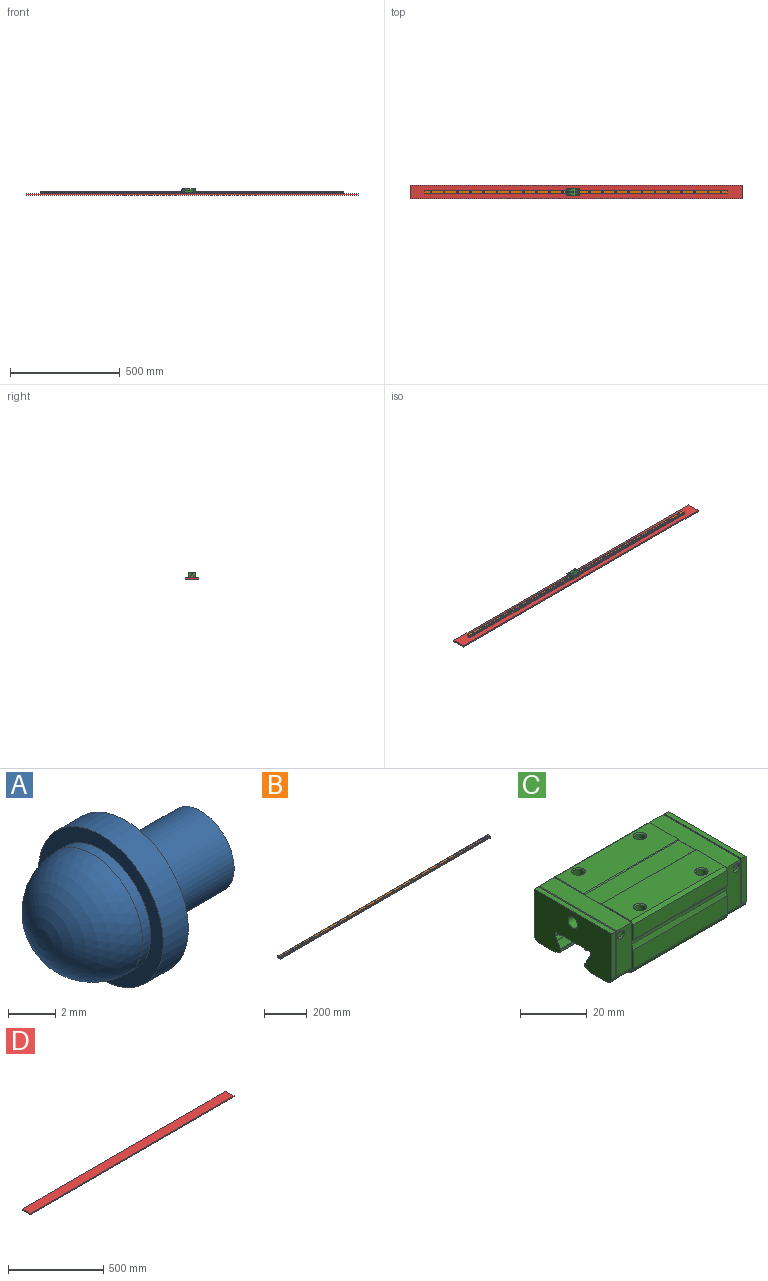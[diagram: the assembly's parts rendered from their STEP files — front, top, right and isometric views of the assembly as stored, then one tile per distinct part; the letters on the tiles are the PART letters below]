
ASSEMBLY  parts=4 mates=3
PART A: 7 faces, bbox 9.5x7.5x7.5 mm
  f0: sphere r=3mm, area 56.5mm2, adj f1
  f1: cylinder r=3mm len=6mm, axis (1,0,0), area 9.4mm2, adj f0,f2
  f2: plane 7.5x7.5mm, normal (-1,0,0), area 15.9mm2, adj f1,f3
  f3: cylinder r=3.75mm len=7.5mm, axis (1,0,0), area 35.3mm2, adj f2,f4
  f4: plane 7.5x7.5mm, normal (1,0,0), area 31.6mm2, adj f3,f5
  f5: cylinder r=2mm len=4.5mm, axis (1,0,0), area 56.5mm2, adj f4,f6
  f6: plane 4x4mm, normal (1,0,0), area 12.6mm2, adj f5
PART B: 97 faces, bbox 1380x15x12.5 mm
  f0: plane 1380x3.92mm, normal (0,-1,0), area 5405.5mm2, adj f1,f25,f26,f27
  f1: plane 1380x0.85mm, normal (0,-0.71,-0.71), area 1658.9mm2, adj f0,f2,f26,f27
  f2: plane 1380x13.3mm, normal (0,0,-1), area 17988.2mm2, adj f1,f3,f26,f27,f30,f33,f36,f39
  f3: plane 1380x0.85mm, normal (0,0.71,-0.71), area 1658.9mm2, adj f2,f4,f26,f27
  f4: plane 1380x3.92mm, normal (0,1,0), area 5405.5mm2, adj f3,f5,f26,f27
  f5: plane 1380x1.85mm, normal (0,0.52,0.86), area 2989.3mm2, adj f4,f6,f26,f27
  f6: cylinder r=0.7mm len=1380mm, axis (-1,0,0), area 1858.8mm2, adj f5,f7,f26,f27
  f7: cylinder r=0.7mm len=1380mm, axis (-1,0,0), area 462mm2, adj f6,f8,f26,f27
  f8: plane 1380x2.43mm, normal (0,0.87,-0.5), area 3876.2mm2, adj f7,f9,f26,f27
  f9: cylinder r=1.45mm len=1380mm, axis (-1,0,0), area 1949.3mm2, adj f8,f10,f26,f27
  f10: plane 1380x0.16mm, normal (0,0.85,-0.52), area 253.7mm2, adj f9,f11,f26,f27
  f11: plane 1380x1.08mm, normal (0,1,0), area 1490.4mm2, adj f10,f12,f26,f27
  f12: plane 1380x0.45mm, normal (0,0.71,0.71), area 878.2mm2, adj f11,f13,f26,f27
  f13: plane 1380x0.38mm, normal (0,0,1), area 529.8mm2, adj f12,f14,f26,f27
  f14: cylinder r=1.45mm len=1380mm, axis (-1,0,0), area 2719.1mm2, adj f13,f15,f26,f27
  f15: plane 1380x9.69mm, normal (0,0,1), area 12353mm2, adj f14,f16,f26,f27,f28,f31,f34,f37
  f16: cylinder r=1.45mm len=1380mm, axis (-1,0,0), area 2719.1mm2, adj f15,f17,f26,f27
  f17: plane 1380x0.38mm, normal (0,0,1), area 529.8mm2, adj f16,f18,f26,f27
  f18: plane 1380x0.45mm, normal (0,-0.71,0.71), area 878.2mm2, adj f17,f19,f26,f27
  f19: plane 1380x1.08mm, normal (0,-1,0), area 1490.4mm2, adj f18,f20,f26,f27
  f20: plane 1380x0.16mm, normal (0,-0.85,-0.52), area 253.7mm2, adj f19,f21,f26,f27
  f21: cylinder r=1.45mm len=1380mm, axis (-1,0,0), area 1949.3mm2, adj f20,f22,f26,f27
  f22: plane 1380x2.43mm, normal (0,-0.87,-0.5), area 3876.2mm2, adj f21,f23,f26,f27
  f23: cylinder r=0.7mm len=1380mm, axis (-1,0,0), area 462mm2, adj f22,f24,f26,f27
  f24: cylinder r=0.7mm len=1380mm, axis (-1,0,0), area 1858.8mm2, adj f23,f25,f26,f27
  f25: plane 1380x1.85mm, normal (0,-0.52,0.86), area 2989.3mm2, adj f0,f24,f26,f27
  f26: plane 15x12.5mm, normal (1,0,0), area 168.5mm2, adj f0,f1,f2,f3,f4,f5,f6,f7
  f27: plane 15x12.5mm, normal (-1,0,0), area 168.5mm2, adj f0,f1,f2,f3,f4,f5,f6,f7
  f28: cylinder r=3.75mm len=7.5mm, axis (0,0,-1), area 124.9mm2, adj f15,f29
  f29: plane 7.5x7.5mm, normal (0,0,1), area 28.3mm2, adj f28,f30
  f30: cylinder r=2.25mm len=7.2mm, axis (0,0,-1), area 101.8mm2, adj f2,f29
  f31: cylinder r=3.75mm len=7.5mm, axis (0,0,-1), area 124.9mm2, adj f15,f32
  f32: plane 7.5x7.5mm, normal (0,0,1), area 28.3mm2, adj f31,f33
  f33: cylinder r=2.25mm len=7.2mm, axis (0,0,-1), area 101.8mm2, adj f2,f32
  f34: cylinder r=3.75mm len=7.5mm, axis (0,0,-1), area 124.9mm2, adj f15,f35
  f35: plane 7.5x7.5mm, normal (0,0,1), area 28.3mm2, adj f34,f36
  f36: cylinder r=2.25mm len=7.2mm, axis (0,0,-1), area 101.8mm2, adj f2,f35
  f37: cylinder r=3.75mm len=7.5mm, axis (0,0,-1), area 124.9mm2, adj f15,f38
  f38: plane 7.5x7.5mm, normal (0,0,1), area 28.3mm2, adj f37,f39
  f39: cylinder r=2.25mm len=7.2mm, axis (0,0,-1), area 101.8mm2, adj f2,f38
  f40: cylinder r=3.75mm len=7.5mm, axis (0,0,-1), area 124.9mm2, adj f15,f41
  f41: plane 7.5x7.5mm, normal (0,0,1), area 28.3mm2, adj f40,f42
  f42: cylinder r=2.25mm len=7.2mm, axis (0,0,-1), area 101.8mm2, adj f2,f41
  f43: cylinder r=3.75mm len=7.5mm, axis (0,0,-1), area 124.9mm2, adj f15,f44
  f44: plane 7.5x7.5mm, normal (0,0,1), area 28.3mm2, adj f43,f45
  f45: cylinder r=2.25mm len=7.2mm, axis (0,0,-1), area 101.8mm2, adj f2,f44
  f46: cylinder r=3.75mm len=7.5mm, axis (0,0,-1), area 124.9mm2, adj f15,f47
  f47: plane 7.5x7.5mm, normal (0,0,1), area 28.3mm2, adj f46,f48
  f48: cylinder r=2.25mm len=7.2mm, axis (0,0,-1), area 101.8mm2, adj f2,f47
  f49: cylinder r=3.75mm len=7.5mm, axis (0,0,-1), area 124.9mm2, adj f15,f50
  f50: plane 7.5x7.5mm, normal (0,0,1), area 28.3mm2, adj f49,f51
  f51: cylinder r=2.25mm len=7.2mm, axis (0,0,-1), area 101.8mm2, adj f2,f50
  f52: cylinder r=3.75mm len=7.5mm, axis (0,0,-1), area 124.9mm2, adj f15,f53
  f53: plane 7.5x7.5mm, normal (0,0,1), area 28.3mm2, adj f52,f54
  f54: cylinder r=2.25mm len=7.2mm, axis (0,0,-1), area 101.8mm2, adj f2,f53
  f55: cylinder r=3.75mm len=7.5mm, axis (0,0,-1), area 124.9mm2, adj f15,f56
  f56: plane 7.5x7.5mm, normal (0,0,1), area 28.3mm2, adj f55,f57
  f57: cylinder r=2.25mm len=7.2mm, axis (0,0,-1), area 101.8mm2, adj f2,f56
  f58: cylinder r=3.75mm len=7.5mm, axis (0,0,-1), area 124.9mm2, adj f15,f59
  f59: plane 7.5x7.5mm, normal (0,0,1), area 28.3mm2, adj f58,f60
  f60: cylinder r=2.25mm len=7.2mm, axis (0,0,-1), area 101.8mm2, adj f2,f59
  f61: cylinder r=3.75mm len=7.5mm, axis (0,0,-1), area 124.9mm2, adj f15,f62
  f62: plane 7.5x7.5mm, normal (0,0,1), area 28.3mm2, adj f61,f63
  f63: cylinder r=2.25mm len=7.2mm, axis (0,0,-1), area 101.8mm2, adj f2,f62
  f64: cylinder r=3.75mm len=7.5mm, axis (0,0,-1), area 124.9mm2, adj f15,f65
  f65: plane 7.5x7.5mm, normal (0,0,1), area 28.3mm2, adj f64,f66
  f66: cylinder r=2.25mm len=7.2mm, axis (0,0,-1), area 101.8mm2, adj f2,f65
  f67: cylinder r=3.75mm len=7.5mm, axis (0,0,-1), area 124.9mm2, adj f15,f68
  f68: plane 7.5x7.5mm, normal (0,0,1), area 28.3mm2, adj f67,f69
  f69: cylinder r=2.25mm len=7.2mm, axis (0,0,-1), area 101.8mm2, adj f2,f68
  f70: cylinder r=3.75mm len=7.5mm, axis (0,0,-1), area 124.9mm2, adj f15,f71
  f71: plane 7.5x7.5mm, normal (0,0,1), area 28.3mm2, adj f70,f72
  f72: cylinder r=2.25mm len=7.2mm, axis (0,0,-1), area 101.8mm2, adj f2,f71
  f73: cylinder r=3.75mm len=7.5mm, axis (0,0,-1), area 124.9mm2, adj f15,f74
  f74: plane 7.5x7.5mm, normal (0,0,1), area 28.3mm2, adj f73,f75
  f75: cylinder r=2.25mm len=7.2mm, axis (0,0,-1), area 101.8mm2, adj f2,f74
  f76: cylinder r=3.75mm len=7.5mm, axis (0,0,-1), area 124.9mm2, adj f15,f77
  f77: plane 7.5x7.5mm, normal (0,0,1), area 28.3mm2, adj f76,f78
  f78: cylinder r=2.25mm len=7.2mm, axis (0,0,-1), area 101.8mm2, adj f2,f77
  f79: cylinder r=3.75mm len=7.5mm, axis (0,0,-1), area 124.9mm2, adj f15,f80
  f80: plane 7.5x7.5mm, normal (0,0,1), area 28.3mm2, adj f79,f81
  f81: cylinder r=2.25mm len=7.2mm, axis (0,0,-1), area 101.8mm2, adj f2,f80
  f82: cylinder r=3.75mm len=7.5mm, axis (0,0,-1), area 124.9mm2, adj f15,f83
  f83: plane 7.5x7.5mm, normal (0,0,1), area 28.3mm2, adj f82,f84
  f84: cylinder r=2.25mm len=7.2mm, axis (0,0,-1), area 101.8mm2, adj f2,f83
  f85: cylinder r=3.75mm len=7.5mm, axis (0,0,-1), area 124.9mm2, adj f15,f86
  f86: plane 7.5x7.5mm, normal (0,0,1), area 28.3mm2, adj f85,f87
  f87: cylinder r=2.25mm len=7.2mm, axis (0,0,-1), area 101.8mm2, adj f2,f86
  f88: cylinder r=3.75mm len=7.5mm, axis (0,0,-1), area 124.9mm2, adj f15,f89
  f89: plane 7.5x7.5mm, normal (0,0,1), area 28.3mm2, adj f88,f90
  f90: cylinder r=2.25mm len=7.2mm, axis (0,0,-1), area 101.8mm2, adj f2,f89
  f91: cylinder r=3.75mm len=7.5mm, axis (0,0,-1), area 124.9mm2, adj f15,f92
  f92: plane 7.5x7.5mm, normal (0,0,1), area 28.3mm2, adj f91,f93
  f93: cylinder r=2.25mm len=7.2mm, axis (0,0,-1), area 101.8mm2, adj f2,f92
  f94: cylinder r=3.75mm len=7.5mm, axis (0,0,-1), area 124.9mm2, adj f15,f95
  f95: plane 7.5x7.5mm, normal (0,0,1), area 28.3mm2, adj f94,f96
  f96: cylinder r=2.25mm len=7.2mm, axis (0,0,-1), area 101.8mm2, adj f2,f95
PART C: 100 faces, bbox 56.9x34x19.5 mm
  f0: plane 16.6x6.3mm, normal (0,-1,0), area 97.5mm2, adj f4,f15,f24,f76,f98
  f1: plane 16.6x1.7mm, normal (0,-1,0), area 28.2mm2, adj f4,f25,f31,f73
  f2: plane 16.6x6.3mm, normal (0,1,0), area 97.5mm2, adj f5,f15,f24,f80,f99
  f3: plane 16.6x1.7mm, normal (0,1,0), area 28.2mm2, adj f5,f25,f31,f73
  f4: cylinder r=2mm len=8.5mm, axis (1,0,0), area 26.2mm2, adj f0,f1,f15,f30,f31,f73,f98
  f5: cylinder r=2mm len=8.5mm, axis (1,0,0), area 26.2mm2, adj f2,f3,f15,f29,f31,f73,f99
  f6: plane 32.8x0.5mm, normal (0.71,0,0.71), area 22.8mm2, adj f24,f73,f98,f99
  f7: plane 16.6x6.3mm, normal (0,-1,0), area 97.5mm2, adj f11,f14,f27,f74,f97
  f8: plane 16.6x1.7mm, normal (0,-1,0), area 28.2mm2, adj f11,f26,f28,f72
  f9: plane 16.6x1.7mm, normal (0,1,0), area 28.2mm2, adj f12,f26,f28,f72
  f10: plane 16.6x6.3mm, normal (0,1,0), area 97.5mm2, adj f12,f14,f27,f78,f96
  f11: cylinder r=2mm len=8.5mm, axis (-1,0,0), area 26.2mm2, adj f7,f8,f14,f28,f30,f72,f97
  f12: cylinder r=2mm len=8.5mm, axis (-1,0,0), area 26.2mm2, adj f9,f10,f14,f28,f29,f72,f96
  f13: plane 32.8x0.5mm, normal (-0.71,0,0.71), area 22.8mm2, adj f27,f72,f96,f97
  f14: plane 34x19.5mm, normal (-1,0,0), area 38.1mm2, adj f7,f10,f11,f12,f16,f17,f20,f21
  f15: plane 34x19.5mm, normal (1,0,0), area 38.1mm2, adj f0,f2,f4,f5,f16,f17,f20,f21
  f16: plane 39.9x5.95mm, normal (0,0,-1), area 237.2mm2, adj f14,f15,f33,f94
  f17: plane 39.9x5.95mm, normal (0,0,-1), area 237.2mm2, adj f14,f15,f34,f95
  f18: plane 56.9x1.47mm, normal (0,-0.52,-0.86), area 97.6mm2, adj f28,f29,f31,f53
  f19: plane 56.9x1.47mm, normal (0,0.52,-0.86), area 97.6mm2, adj f28,f30,f31,f71
  f20: plane 39.9x6.69mm, normal (0,-1,0), area 266.9mm2, adj f14,f15,f33,f92
  f21: plane 39.9x5.52mm, normal (0,-1,0), area 220.2mm2, adj f14,f15,f32,f93
  f22: plane 39.9x6.69mm, normal (0,1,0), area 266.9mm2, adj f14,f15,f34,f88
  f23: plane 39.9x5.52mm, normal (0,1,0), area 220.2mm2, adj f14,f15,f35,f89
  f24: plane 32.8x6.3mm, normal (0,0,1), area 206.6mm2, adj f0,f2,f6,f15
  f25: plane 32.8x1.7mm, normal (0,0,1), area 55.8mm2, adj f1,f3,f31,f73
  f26: plane 32.8x1.7mm, normal (0,0,1), area 55.8mm2, adj f8,f9,f28,f72
  f27: plane 32.8x6.3mm, normal (0,0,1), area 206.6mm2, adj f7,f10,f13,f14
  f28: plane 32.8x18.6mm, normal (-1,0,0), area 501.5mm2, adj f8,f9,f11,f12,f18,f19,f26,f29
  f29: plane 56.9x7.29mm, normal (0,0,-1), area 146.6mm2, adj f5,f12,f14,f15,f18,f28,f31,f95
  f30: plane 56.9x7.29mm, normal (0,0,-1), area 146.6mm2, adj f4,f11,f14,f15,f19,f28,f31,f94
  f31: plane 32.8x18.6mm, normal (1,0,0), area 501.5mm2, adj f1,f3,f4,f5,f18,f19,f25,f29
  f32: plane 39.9x0.98mm, normal (0,-0.71,0.71), area 55.3mm2, adj f14,f15,f21,f40
  f33: cylinder r=2.5mm len=39.9mm, axis (-1,0,0), area 156.7mm2, adj f14,f15,f16,f20
  f34: cylinder r=2.5mm len=39.9mm, axis (-1,0,0), area 156.7mm2, adj f14,f15,f17,f22
  f35: plane 39.9x0.98mm, normal (0,0.71,0.71), area 55.3mm2, adj f14,f15,f23,f36
  f36: plane 39.9x12.22mm, normal (0,0,1), area 462.4mm2, adj f14,f15,f35,f37,f47,f50
  f37: plane 39.9x0.3mm, normal (0,-0.71,0.71), area 16.9mm2, adj f14,f15,f36,f38
  f38: plane 39.9x7mm, normal (0,0,1), area 279.3mm2, adj f14,f15,f37,f39
  f39: plane 39.9x0.3mm, normal (0,0.71,0.71), area 16.9mm2, adj f14,f15,f38,f40
  f40: plane 39.9x12.22mm, normal (0,0,1), area 462.4mm2, adj f14,f15,f32,f39,f41,f44
  f41: cone r=2mm half-angle=45deg, axis (0,0,1), area 6.1mm2, adj f40,f42
  f42: cylinder r=1.62mm len=8.02mm, axis (0,0,-1), area 81.7mm2, adj f41,f43
  f43: cone r=1.62mm half-angle=60deg, axis (0,0,1), area 9.5mm2, adj f42
  f44: cone r=2mm half-angle=45deg, axis (0,0,1), area 6.1mm2, adj f40,f45
  f45: cylinder r=1.62mm len=8.02mm, axis (0,0,-1), area 81.7mm2, adj f44,f46
  f46: cone r=1.62mm half-angle=60deg, axis (0,0,1), area 9.5mm2, adj f45
  f47: cone r=2mm half-angle=45deg, axis (0,0,1), area 6.1mm2, adj f36,f48
  f48: cylinder r=1.62mm len=8.02mm, axis (0,0,-1), area 81.7mm2, adj f47,f49
  f49: cone r=1.62mm half-angle=60deg, axis (0,0,1), area 9.5mm2, adj f48
  f50: cone r=2mm half-angle=45deg, axis (0,0,1), area 6.1mm2, adj f36,f51
  f51: cylinder r=1.62mm len=8.02mm, axis (0,0,-1), area 81.7mm2, adj f50,f52
  f52: cone r=1.62mm half-angle=60deg, axis (0,0,1), area 9.5mm2, adj f51
  f53: cylinder r=0.7mm len=56.9mm, axis (-1,0,0), area 76.6mm2, adj f18,f28,f31,f54
  f54: cylinder r=0.7mm len=56.9mm, axis (-1,0,0), area 19mm2, adj f28,f31,f53,f55
  f55: plane 56.9x2.43mm, normal (0,-0.87,0.5), area 159.8mm2, adj f28,f31,f54,f56
  f56: cylinder r=1.45mm len=56.9mm, axis (-1,0,0), area 80.4mm2, adj f28,f31,f55,f57
  f57: plane 56.9x0.16mm, normal (0,-0.85,0.52), area 10.5mm2, adj f28,f31,f56,f58
  f58: plane 56.9x1.08mm, normal (0,-1,0), area 61.5mm2, adj f28,f31,f57,f59
  f59: plane 56.9x0.45mm, normal (0,-0.71,-0.71), area 36.2mm2, adj f28,f31,f58,f60
  f60: plane 56.9x0.38mm, normal (0,0,-1), area 21.8mm2, adj f28,f31,f59,f61
  f61: cylinder r=1.45mm len=56.9mm, axis (-1,0,0), area 112.1mm2, adj f28,f31,f60,f62
  f62: plane 56.9x9.69mm, normal (0,0,-1), area 551.2mm2, adj f28,f31,f61,f63
  f63: cylinder r=1.45mm len=56.9mm, axis (-1,0,0), area 112.1mm2, adj f28,f31,f62,f64
  f64: plane 56.9x0.38mm, normal (0,0,-1), area 21.8mm2, adj f28,f31,f63,f65
  f65: plane 56.9x0.45mm, normal (0,0.71,-0.71), area 36.2mm2, adj f28,f31,f64,f66
  f66: plane 56.9x1.08mm, normal (0,1,0), area 61.5mm2, adj f28,f31,f65,f67
  f67: plane 56.9x0.16mm, normal (0,0.85,0.52), area 10.5mm2, adj f28,f31,f66,f68
  f68: cylinder r=1.45mm len=56.9mm, axis (-1,0,0), area 80.4mm2, adj f28,f31,f67,f69
  f69: plane 56.9x2.43mm, normal (0,0.87,0.5), area 159.8mm2, adj f28,f31,f68,f70
  f70: cylinder r=0.7mm len=56.9mm, axis (-1,0,0), area 19mm2, adj f28,f31,f69,f71
  f71: cylinder r=0.7mm len=56.9mm, axis (-1,0,0), area 76.6mm2, adj f19,f28,f31,f70
  f72: plane 32.8x17.92mm, normal (1,0,0), area 33.4mm2, adj f8,f9,f11,f12,f13,f26,f96,f97
  f73: plane 32.8x17.92mm, normal (-1,0,0), area 33.4mm2, adj f1,f3,f4,f5,f6,f25,f98,f99
  f74: cylinder r=1.5mm len=3mm, axis (0,-1,0), area 9.4mm2, adj f7,f75
  f75: plane 3x3mm, normal (0,-1,0), area 7.1mm2, adj f74
  f76: cylinder r=1.5mm len=3mm, axis (0,-1,0), area 9.4mm2, adj f0,f77
  f77: plane 3x3mm, normal (0,-1,0), area 7.1mm2, adj f76
  f78: cylinder r=1.5mm len=3mm, axis (0,1,0), area 9.4mm2, adj f10,f79
  f79: plane 3x3mm, normal (0,1,0), area 7.1mm2, adj f78
  f80: cylinder r=1.5mm len=3mm, axis (0,1,0), area 9.4mm2, adj f2,f81
  f81: plane 3x3mm, normal (0,1,0), area 7.1mm2, adj f80
  f82: cylinder r=2mm len=4.5mm, axis (1,0,0), area 56.5mm2, adj f28,f83
  f83: plane 4x4mm, normal (-1,0,0), area 12.6mm2, adj f82
  f84: plane 4x4mm, normal (1,0,0), area 12.6mm2, adj f85
  f85: cylinder r=2mm len=4.5mm, axis (1,0,0), area 56.5mm2, adj f31,f84
  f86: plane 39.9x1.13mm, normal (0,1,0), area 45.2mm2, adj f14,f15,f87,f88
  f87: cylinder r=0.5mm len=39.9mm, axis (-1,0,0), area 12.2mm2, adj f14,f15,f86,f89
  f88: plane 39.9x1.81mm, normal (0,0.96,0.27), area 74.9mm2, adj f14,f15,f22,f86
  f89: plane 39.9x0.58mm, normal (0,0.82,-0.58), area 28.3mm2, adj f14,f15,f23,f87
  f90: plane 39.9x1.13mm, normal (0,-1,0), area 45.2mm2, adj f14,f15,f91,f92
  f91: cylinder r=0.5mm len=39.9mm, axis (-1,0,0), area 12.2mm2, adj f14,f15,f90,f93
  f92: plane 39.9x1.81mm, normal (0,-0.96,0.27), area 74.9mm2, adj f14,f15,f20,f90
  f93: plane 39.9x0.58mm, normal (0,-0.82,-0.58), area 28.3mm2, adj f14,f15,f21,f91
  f94: plane 39.9x0.87mm, normal (0,0.5,-0.87), area 40mm2, adj f14,f15,f16,f30
  f95: plane 39.9x0.87mm, normal (0,-0.5,-0.87), area 40mm2, adj f14,f15,f17,f29
  f96: plane 17.92x0.5mm, normal (-0.71,0.71,0), area 12.2mm2, adj f10,f12,f13,f72
  f97: plane 17.92x0.5mm, normal (-0.71,-0.71,0), area 12.2mm2, adj f7,f11,f13,f72
  f98: plane 17.92x0.5mm, normal (0.71,-0.71,0), area 12.2mm2, adj f0,f4,f6,f73
  f99: plane 17.92x0.5mm, normal (0.71,0.71,0), area 12.2mm2, adj f2,f5,f6,f73
PART D: 6 faces, bbox 1510x60x6.4 mm
  f0: plane 1510x6.35mm, normal (0,-1,0), area 9588.5mm2, adj f1,f3,f4,f5
  f1: plane 60x6.35mm, normal (1,0,0), area 381mm2, adj f0,f2,f4,f5
  f2: plane 1510x6.35mm, normal (0,1,0), area 9588.5mm2, adj f1,f3,f4,f5
  f3: plane 60x6.35mm, normal (-1,0,0), area 381mm2, adj f0,f2,f4,f5
  f4: plane 1510x60mm, normal (0,0,1), area 90600mm2, adj f0,f1,f2,f3
  f5: plane 1510x60mm, normal (0,0,-1), area 90600mm2, adj f0,f1,f2,f3
PLACE A t=(617.41,29.8,7.73)mm
PLACE B t=(0,29.8,-11.77)mm fixed
PLACE C t=(645.86,29.8,-7.27)mm
PLACE D t=(660,29.8,-18.12)mm
MATE fastened C.f82 <-> A.f1  axis (-1,0,0) through (617.41,29.8,7.73)mm
MATE slider C.f63 <-> B.f16  axis (-1,0,0) through (645.86,24.04,1.86)mm
MATE fastened B.f61 <-> D.f4  axis (0,0,-1) through (660,29.8,-11.77)mm
